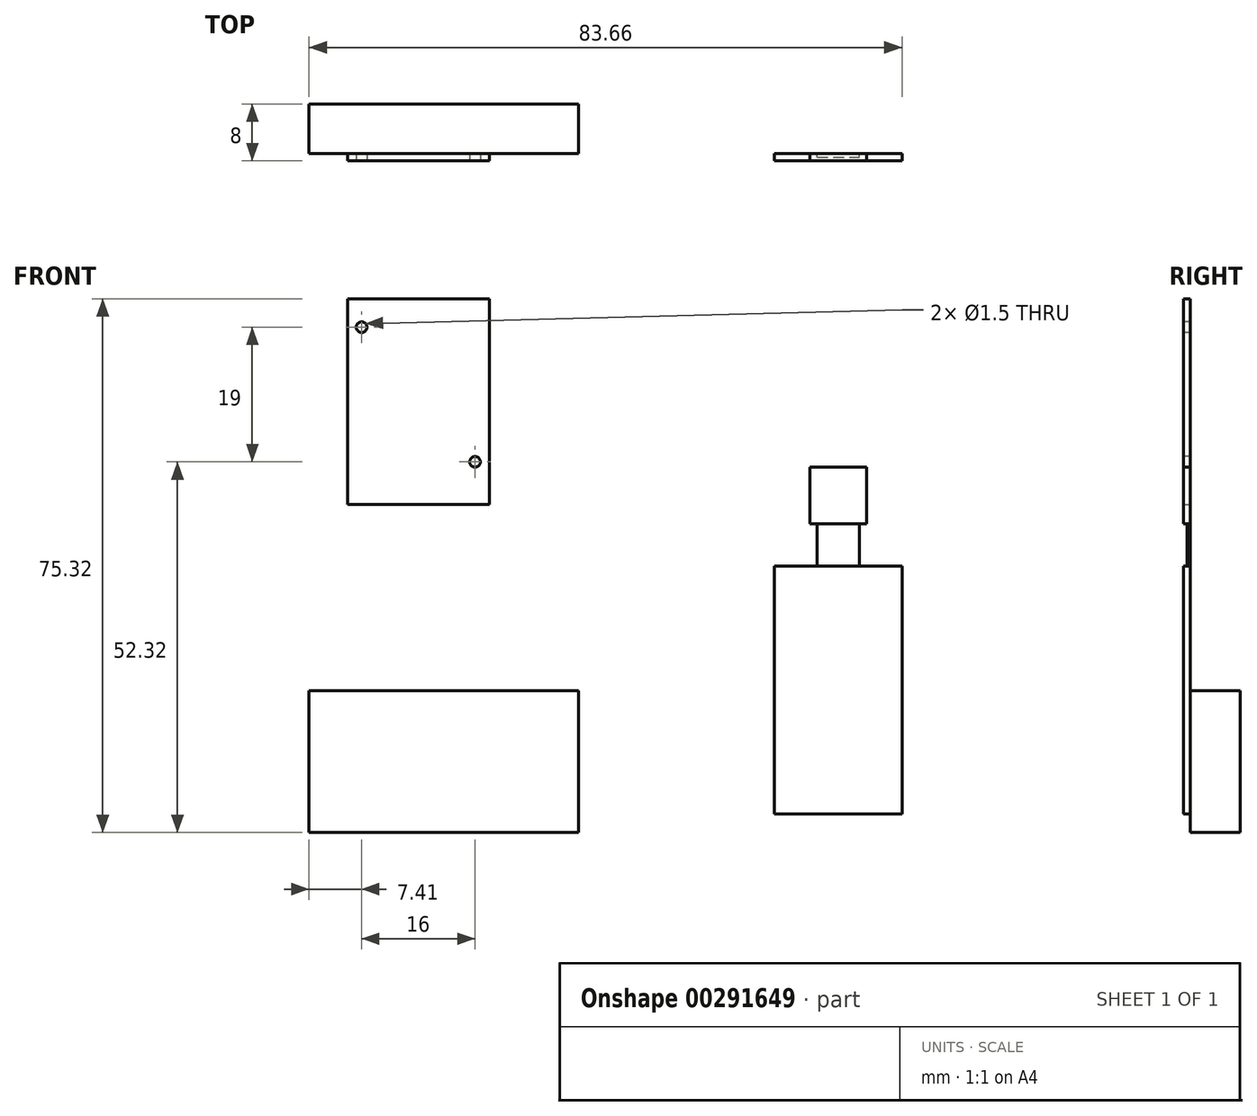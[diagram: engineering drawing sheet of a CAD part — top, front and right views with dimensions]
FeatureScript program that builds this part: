
annotation { "Feature Type Name" : "Feature", "Feature Type Description" : "" }
export const myFeature = defineFeature(function(context is Context, id is Id, definition is map)
    precondition{}
    {
        {
            var Q0;
            Q0=qCreatedBy(makeId("Front.planeOp"),FACE);
            var sketch = newSketch(context, id + "F0", { "sketchPlane" : qUnion([Q0])});
            skLineSegment(sketch, "E0.bottom", {"start": v(0, 0) * mm, "end": v(-20, 0) * mm});
            skLineSegment(sketch, "E0.top", {"start": v(0, 29) * mm, "end": v(-20, 29) * mm});
            skLineSegment(sketch, "E0.left", {"start": v(0, 0) * mm, "end": v(0, 29) * mm});
            skLineSegment(sketch, "E0.right", {"start": v(-20, 0) * mm, "end": v(-20, 29) * mm});
            skSolve(sketch);
        }
        {
            var Q0;
            Q0=makeQuery(id+"F0.imprint","IMPRINT",FACE,{"disambiguationData":[TD([[makeQuery(id+"F0.imprint","IMPRINT",EDGE,{"derivedFrom":sQuery(id+"F0.wireOp",EDGE,"E0.bottom")}),-1.0]])]});
            extrude(context, id + "F1", {"entities" : qUnion([Q0]), "depth" : 1 * mm});
        }
        {
            var Q0;
            Q0=makeQuery(id+"F1.opExtrude","CAP_FACE",FACE,{"disambiguationData":[OSD([sQuery(id+"F0.wireOp",EDGE,"E0.bottom"),sQuery(id+"F0.wireOp",EDGE,"E0.top"),sQuery(id+"F0.wireOp",EDGE,"E0.left"),sQuery(id+"F0.wireOp",EDGE,"E0.right")])],"isStart":false});
            var sketch = newSketch(context, id + "F2", { "sketchPlane" : qUnion([Q0])});
            skCircle(sketch, "E1", {"center": v(-2, 6) * mm, "radius": 0.75 * mm});
            skCircle(sketch, "E2", {"center": v(-18, 25) * mm, "radius": 0.75 * mm});
            skSolve(sketch);
        }
        {
            var Q0;
            Q0 = qSketchRegion(id + "F2", true);
            extrude(context, id + "F3", {"entities" : qUnion([Q0]), "operationType" : NewBodyOperationType.REMOVE, "oppositeDirection" : true, "depth" : 25 * mm});
        }
        {
            var Q0;
            Q0=qCreatedBy(makeId("Front.planeOp"),FACE);
            var sketch = newSketch(context, id + "F4", { "sketchPlane" : qUnion([Q0])});
            skLineSegment(sketch, "E3.bottom", {"start": v(58.25, -43.73) * mm, "end": v(40.25, -43.73) * mm});
            skLineSegment(sketch, "E3.top", {"start": v(58.25, -8.73) * mm, "end": v(40.25, -8.73) * mm});
            skLineSegment(sketch, "E3.left", {"start": v(58.25, -43.73) * mm, "end": v(58.25, -8.73) * mm});
            skLineSegment(sketch, "E3.right", {"start": v(40.25, -43.73) * mm, "end": v(40.25, -8.73) * mm});
            skLineSegment(sketch, "E4.bottom", {"start": v(52.25, -8.73) * mm, "end": v(46.25, -8.73) * mm});
            skLineSegment(sketch, "E4.left", {"start": v(52.25, -8.73) * mm, "end": v(52.25, -2.73) * mm});
            skLineSegment(sketch, "E4.right", {"start": v(46.25, -8.73) * mm, "end": v(46.25, -2.73) * mm});
            skLineSegment(sketch, "E5", {"start": v(46.25, -2.73) * mm, "end": v(45.25, -2.73) * mm});
            skLineSegment(sketch, "E6", {"start": v(45.25, -2.73) * mm, "end": v(45.25, 6.25) * mm});
            skLineSegment(sketch, "E7.bottom", {"start": v(45.25, -2.73) * mm, "end": v(53.25, -2.73) * mm});
            skLineSegment(sketch, "E7.top", {"start": v(45.25, 5.27) * mm, "end": v(53.25, 5.27) * mm});
            skLineSegment(sketch, "E7.left", {"start": v(45.25, -2.73) * mm, "end": v(45.25, 5.27) * mm});
            skLineSegment(sketch, "E7.right", {"start": v(53.25, -2.73) * mm, "end": v(53.25, 5.27) * mm});
            skSolve(sketch);
        }
        {
            var Q0;
            Q0=makeQuery(id+"F4.imprint","IMPRINT",FACE,{"disambiguationData":[TD([[makeQuery(id+"F4.imprint","IMPRINT",EDGE,{"derivedFrom":sQuery(id+"F4.wireOp",EDGE,"E3.bottom")}),-1.0]])]});
            var Q1;
            {var subQ3=sQuery(id+"F4.wireOp",EDGE,"E5");Q1=makeQuery(id+"F4.imprint","IMPRINT",FACE,{"disambiguationData":[TD([[makeQuery(id+"F4.imprint","IMPRINT",EDGE,{"derivedFrom":subQ3}),-1.0]])]});}
            extrude(context, id + "F5", {"entities" : qUnion([Q0, Q1]), "depth" : 1 * mm});
        }
        {
            var Q0;
            {var subQ0=sQuery(id+"F4.wireOp",EDGE,"E4.left");Q0=makeQuery(id+"F4.imprint","IMPRINT",FACE,{"disambiguationData":[TD([[makeQuery(id+"F4.imprint","IMPRINT",EDGE,{"derivedFrom":subQ0}),1.0]])]});}
            extrude(context, id + "F6", {"entities" : qUnion([Q0]), "depth" : 0.5 * mm});
        }
        {
            var Q0;
            Q0=qCreatedBy(makeId("Front.planeOp"),FACE);
            var sketch = newSketch(context, id + "F7", { "sketchPlane" : qUnion([Q0])});
            skLineSegment(sketch, "E8.bottom", {"start": v(12.6, -26.32) * mm, "end": v(-25.4, -26.32) * mm});
            skLineSegment(sketch, "E8.top", {"start": v(12.6, -46.32) * mm, "end": v(-25.4, -46.32) * mm});
            skLineSegment(sketch, "E8.left", {"start": v(12.6, -26.32) * mm, "end": v(12.6, -46.32) * mm});
            skLineSegment(sketch, "E8.right", {"start": v(-25.4, -26.32) * mm, "end": v(-25.4, -46.32) * mm});
            skSolve(sketch);
        }
        {
            var Q0;
            Q0 = qSketchRegion(id + "F7", true);
            extrude(context, id + "F8", {"entities" : qUnion([Q0]), "oppositeDirection" : true, "depth" : 7 * mm});
        }
    });
